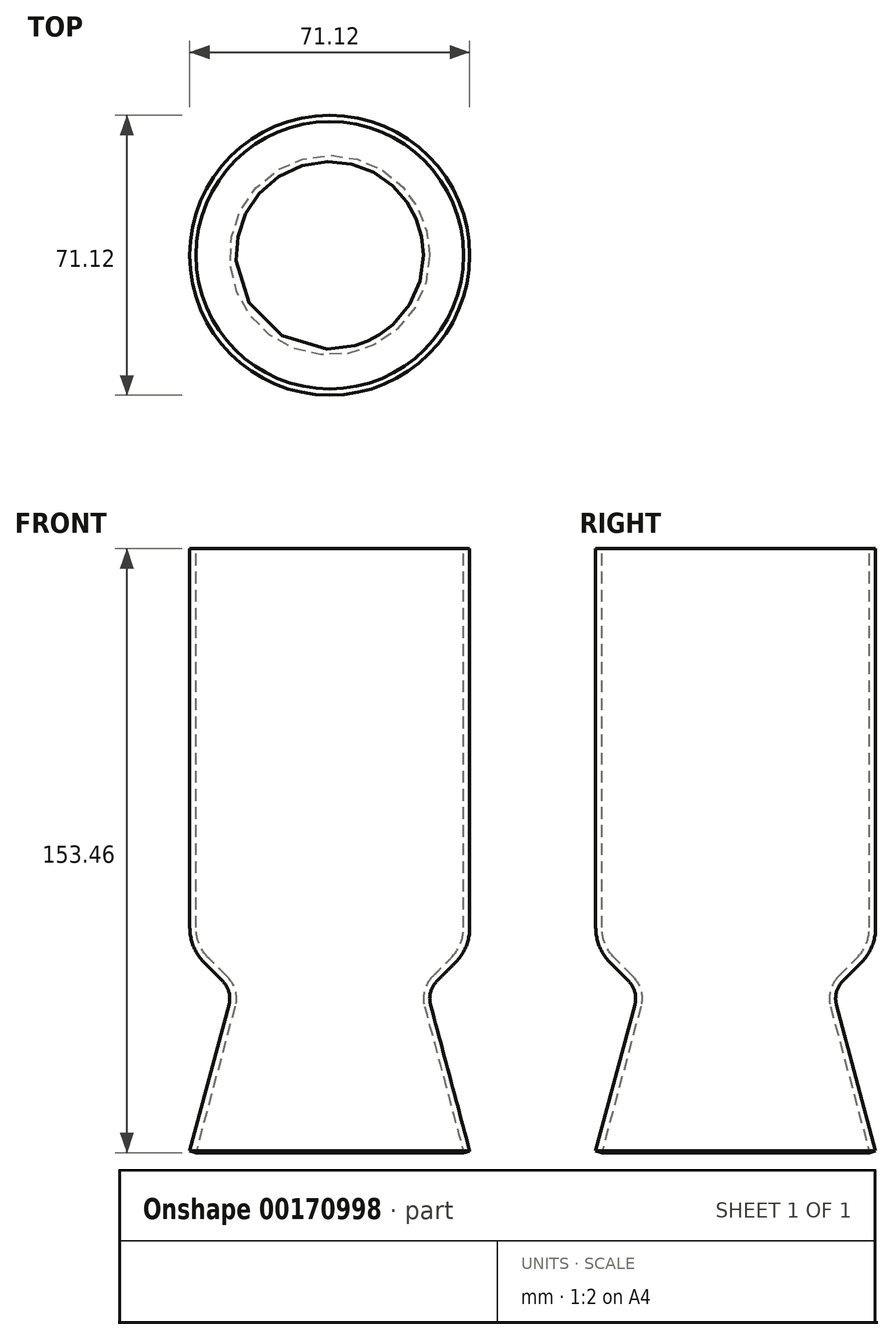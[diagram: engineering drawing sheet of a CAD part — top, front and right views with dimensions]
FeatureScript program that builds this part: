
annotation { "Feature Type Name" : "Feature", "Feature Type Description" : "" }
export const myFeature = defineFeature(function(context is Context, id is Id, definition is map)
    precondition{}
    {
        {
            var Q0;
            Q0=qCreatedBy(makeId("Front.planeOp"),FACE);
            var sketch = newSketch(context, id + "F0", { "sketchPlane" : qUnion([Q0])});
            skLineSegment(sketch, "E0", {"start": v(-35.56, 114.3) * mm, "end": v(-35.56, 18.05) * mm});
            skLineSegment(sketch, "E1", {"start": v(-31.84, 9.07) * mm, "end": v(-27.26, 4.5) * mm});
            skLineSegment(sketch, "E2", {"start": v(-25.62, -1.64) * mm, "end": v(-35.56, -38.75) * mm});
            skPoint(sketch, "E3.visualSharp", {"position": v(-24.67, 1.9) * mm});
            skArc(sketch, "E3.filletArc", {"start": v(-25.62, -1.64) * mm, "mid": v(-25.62, 1.64) * mm, "end": v(-27.26, 4.5) * mm});
            skPoint(sketch, "E4.visualSharp", {"position": v(-35.56, 12.8) * mm});
            skArc(sketch, "E4.filletArc", {"start": v(-35.56, 18.05) * mm, "mid": v(-34.6, 13.2) * mm, "end": v(-31.84, 9.07) * mm});
            skLineSegment(sketch, "E5.0", {"start": v(-24.08, -2.05) * mm, "end": v(-34.03, -39.16) * mm});
            skLineSegment(sketch, "E5.1", {"start": v(-33.97, 114.3) * mm, "end": v(-33.97, 18.05) * mm});
            skArc(sketch, "E5.2", {"start": v(-33.97, 18.05) * mm, "mid": v(-33.13, 13.8) * mm, "end": v(-30.72, 10.2) * mm});
            skLineSegment(sketch, "E5.3", {"start": v(-30.72, 10.2) * mm, "end": v(-26.14, 5.61) * mm});
            skArc(sketch, "E5.4", {"start": v(-24.08, -2.05) * mm, "mid": v(-24.08, 2.05) * mm, "end": v(-26.14, 5.61) * mm});
            skLineSegment(sketch, "E6", {"start": v(-35.56, 114.3) * mm, "end": v(-33.97, 114.3) * mm});
            skLineSegment(sketch, "E7", {"start": v(-34.03, -39.16) * mm, "end": v(-35.56, -38.75) * mm});
            skLineSegment(sketch, "E8", {"start": v(0, 114.3) * mm, "end": v(0, -39.16) * mm});
            skSolve(sketch);
        }
        {
            var Q0;
            Q0 = qSketchRegion(id + "F0", true);
            var Q1;
            Q1=sQuery(id+"F0.wireOp",EDGE,"E8");
            revolve(context, id + "F1", {"entities" : qUnion([Q0]), "axis" : qUnion([Q1]), "revolveType" : RevolveType.FULL});
        }
    });
